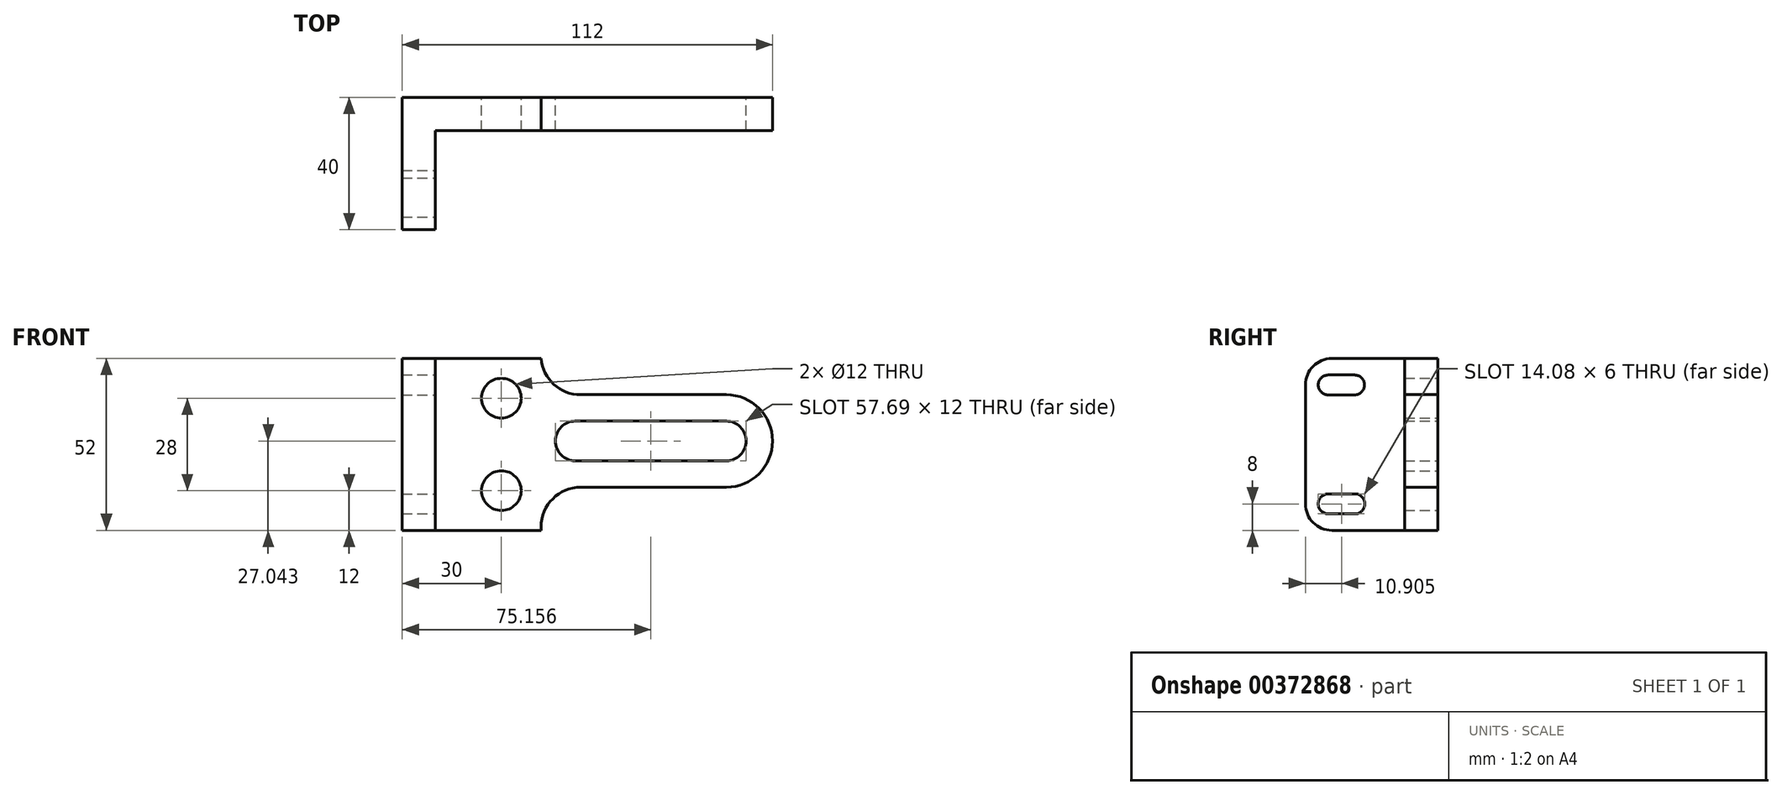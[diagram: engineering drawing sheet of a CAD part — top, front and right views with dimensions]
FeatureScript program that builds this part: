
annotation { "Feature Type Name" : "Feature", "Feature Type Description" : "" }
export const myFeature = defineFeature(function(context is Context, id is Id, definition is map)
    precondition{}
    {
        {
            var Q0;
            Q0=qCreatedBy(makeId("Front.planeOp"),FACE);
            var sketch = newSketch(context, id + "F0", { "sketchPlane" : qUnion([Q0])});
            skLineSegment(sketch, "E0", {"start": v(0, 52) * mm, "end": v(32, 52) * mm});
            skLineSegment(sketch, "E1", {"start": v(32, 0) * mm, "end": v(0, 0) * mm});
            skLineSegment(sketch, "E2", {"start": v(0, 0) * mm, "end": v(0, 52) * mm});
            skLineSegment(sketch, "E3", {"start": v(32, 52) * mm, "end": v(32, 41.04) * mm});
            skLineSegment(sketch, "E4", {"start": v(32, 41.04) * mm, "end": v(88, 41.04) * mm});
            skLineSegment(sketch, "E5", {"start": v(88, 13.04) * mm, "end": v(32, 13.04) * mm});
            skLineSegment(sketch, "E6", {"start": v(32, 13.04) * mm, "end": v(32, 0) * mm});
            skArc(sketch, "E7", {"start": v(88, 13.04) * mm, "mid": v(102, 27.04) * mm, "end": v(88, 41.04) * mm});
            skArc(sketch, "E8", {"start": v(88, 21.04) * mm, "mid": v(94, 27.04) * mm, "end": v(88, 33.04) * mm});
            skArc(sketch, "E9", {"start": v(42.31, 33.04) * mm, "mid": v(36.31, 27.04) * mm, "end": v(42.31, 21.04) * mm});
            skLineSegment(sketch, "E10", {"start": v(88, 21.04) * mm, "end": v(42.31, 21.04) * mm});
            skLineSegment(sketch, "E11", {"start": v(42.31, 33.04) * mm, "end": v(88, 33.04) * mm});
            skCircle(sketch, "E12", {"center": v(20, 40) * mm, "radius": 6 * mm});
            skCircle(sketch, "E13", {"center": v(20, 12) * mm, "radius": 6 * mm});
            skSolve(sketch);
        }
        {
            var Q0;
            Q0 = qSketchRegion(id + "F0", true);
            extrude(context, id + "F1", {"entities" : qUnion([Q0]), "depth" : 10 * mm});
        }
        {
            var Q0;
            Q0=makeQuery(id+"F1.opExtrude","SWEPT_EDGE",EDGE,{"disambiguationData":[OSD([sQuery(id+"F0.wireOp",EDGE,"E3"),sQuery(id+"F0.wireOp",EDGE,"E4")])]});
            var Q1;
            Q1=makeQuery(id+"F1.opExtrude","SWEPT_EDGE",EDGE,{"disambiguationData":[OSD([sQuery(id+"F0.wireOp",EDGE,"E5"),sQuery(id+"F0.wireOp",EDGE,"E6")])]});
            fillet(context, id + "F2", {"entities" : qUnion([Q0, Q1]), "radius" : 12 * mm, "tangentPropagation" : true, "allowEdgeOverflow" : false});
        }
        {
            var Q0;
            Q0=makeQuery(id+"F1.opExtrude","SWEPT_FACE",FACE,{"disambiguationData":[OSD([sQuery(id+"F0.wireOp",EDGE,"E2")])]});
            var sketch = newSketch(context, id + "F3", { "sketchPlane" : qUnion([Q0])});
            skLineSegment(sketch, "E14", {"start": v(0, 52) * mm, "end": v(40, 52) * mm});
            skLineSegment(sketch, "E15", {"start": v(40, 52) * mm, "end": v(40, 0) * mm});
            skLineSegment(sketch, "E16", {"start": v(40, 0) * mm, "end": v(0, 0) * mm});
            skLineSegment(sketch, "E17", {"start": v(0, 0) * mm, "end": v(0, 52) * mm});
            skArc(sketch, "E18", {"start": v(33.14, 41) * mm, "mid": v(36.14, 44) * mm, "end": v(33.14, 47) * mm});
            skArc(sketch, "E19", {"start": v(25.14, 47) * mm, "mid": v(22.14, 44) * mm, "end": v(25.14, 41) * mm});
            skArc(sketch, "E20", {"start": v(33.14, 5) * mm, "mid": v(36.14, 8) * mm, "end": v(33.14, 11) * mm});
            skArc(sketch, "E21", {"start": v(24.43, 11) * mm, "mid": v(22.05, 8) * mm, "end": v(24.43, 5) * mm});
            skLineSegment(sketch, "E22", {"start": v(33.14, 41) * mm, "end": v(25.14, 41) * mm});
            skLineSegment(sketch, "E23", {"start": v(25.14, 47) * mm, "end": v(33.14, 47) * mm});
            skLineSegment(sketch, "E24", {"start": v(33.14, 5) * mm, "end": v(24.43, 5) * mm});
            skLineSegment(sketch, "E25", {"start": v(24.43, 11) * mm, "end": v(33.14, 11) * mm});
            skSolve(sketch);
        }
        {
            var Q0;
            Q0 = qSketchRegion(id + "F3", true);
            extrude(context, id + "F4", {"entities" : qUnion([Q0]), "operationType" : NewBodyOperationType.ADD, "depth" : 10 * mm});
        }
        {
            var Q0;
            Q0=makeQuery(id+"F4.opExtrude","SWEPT_EDGE",EDGE,{"disambiguationData":[OSD([sQuery(id+"F3.wireOp",EDGE,"E14"),sQuery(id+"F3.wireOp",EDGE,"E15")])]});
            var Q1;
            Q1=makeQuery(id+"F4.opExtrude","SWEPT_EDGE",EDGE,{"disambiguationData":[OSD([sQuery(id+"F3.wireOp",EDGE,"E15"),sQuery(id+"F3.wireOp",EDGE,"E16")])]});
            fillet(context, id + "F5", {"entities" : qUnion([Q0, Q1]), "radius" : 8 * mm, "tangentPropagation" : true, "allowEdgeOverflow" : false});
        }
    });
